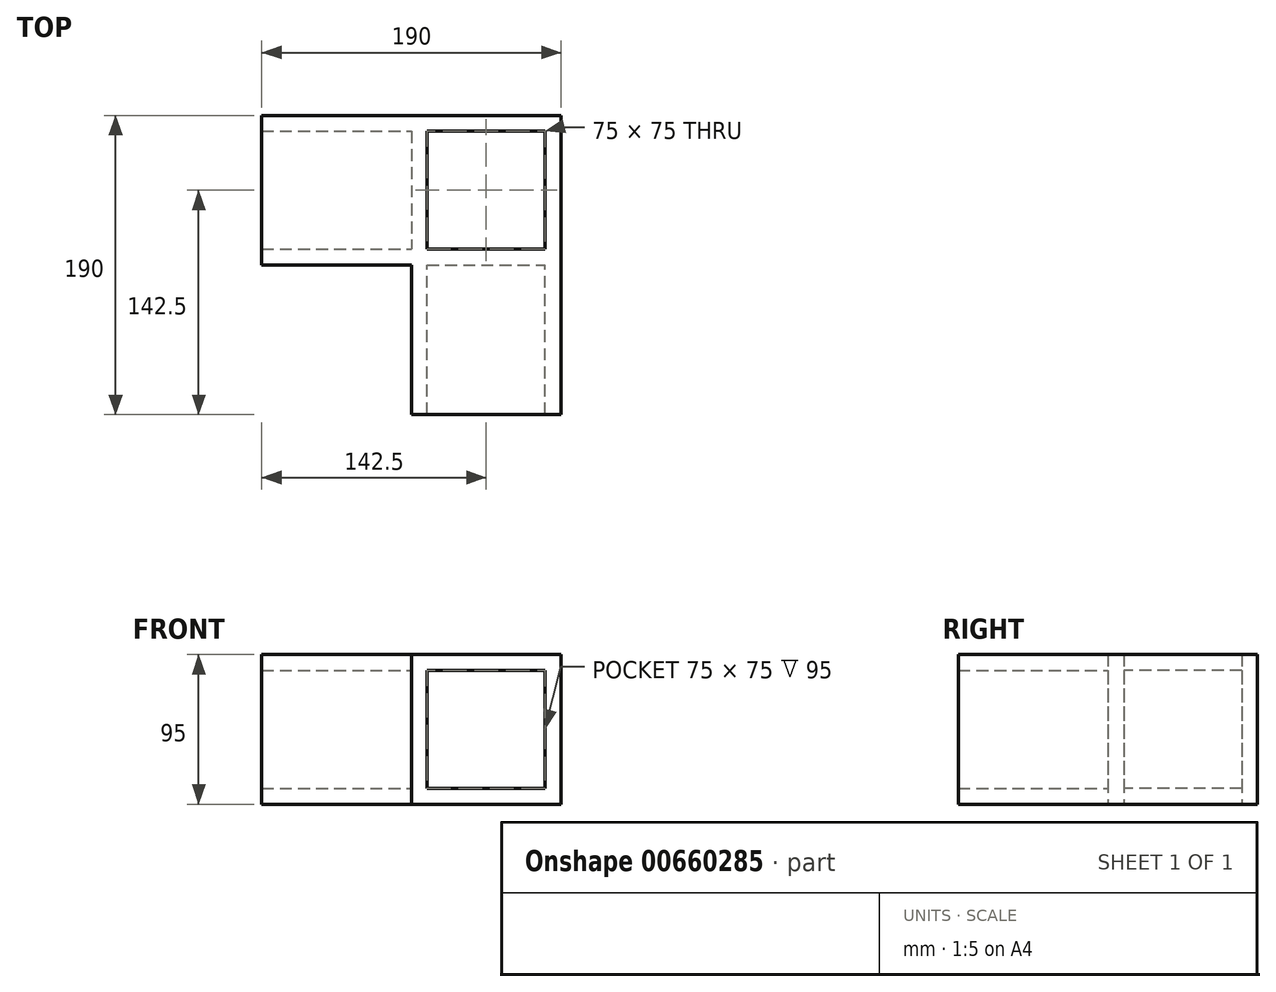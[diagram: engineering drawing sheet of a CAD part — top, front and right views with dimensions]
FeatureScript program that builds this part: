
annotation { "Feature Type Name" : "Feature", "Feature Type Description" : "" }
export const myFeature = defineFeature(function(context is Context, id is Id, definition is map)
    precondition{}
    {
        {
            var Q0;
            Q0=qCreatedBy(makeId("Top.planeOp"),FACE);
            var sketch = newSketch(context, id + "F0", { "sketchPlane" : qUnion([Q0])});
            skLineSegment(sketch, "E0.bottom", {"start": v(37.5, 37.5) * mm, "end": v(-37.5, 37.5) * mm});
            skLineSegment(sketch, "E0.top", {"start": v(37.5, -37.5) * mm, "end": v(-37.5, -37.5) * mm});
            skLineSegment(sketch, "E0.left", {"start": v(37.5, 37.5) * mm, "end": v(37.5, -37.5) * mm});
            skLineSegment(sketch, "E0.right", {"start": v(-37.5, 37.5) * mm, "end": v(-37.5, -37.5) * mm});
            skPoint(sketch, "E0.middle", {"position": v(0, 0) * mm});
            skLineSegment(sketch, "E1.bottom", {"start": v(47.5, 47.5) * mm, "end": v(-47.5, 47.5) * mm});
            skLineSegment(sketch, "E1.top", {"start": v(47.5, -47.5) * mm, "end": v(-47.5, -47.5) * mm});
            skLineSegment(sketch, "E1.left", {"start": v(47.5, 47.5) * mm, "end": v(47.5, -47.5) * mm});
            skLineSegment(sketch, "E1.right", {"start": v(-47.5, 47.5) * mm, "end": v(-47.5, -47.5) * mm});
            skSolve(sketch);
        }
        {
            var Q0;
            Q0 = qSketchRegion(id + "F0", true);
            extrude(context, id + "F1", {"entities" : qUnion([Q0]), "depth" : 95 * mm, "offsetDistance" : 25 * mm});
        }
        {
            var Q0;
            Q0=makeQuery(id+"F1.opExtrude","SWEPT_FACE",FACE,{"disambiguationData":[OSD([sQuery(id+"F0.wireOp",EDGE,"E1.top")])]});
            var sketch = newSketch(context, id + "F2", { "sketchPlane" : qUnion([Q0])});
            skLineSegment(sketch, "E2.bottom", {"start": v(-47.5, 95) * mm, "end": v(47.5, 95) * mm});
            skLineSegment(sketch, "E2.top", {"start": v(-47.5, 0) * mm, "end": v(47.5, 0) * mm});
            skLineSegment(sketch, "E2.left", {"start": v(-47.5, 95) * mm, "end": v(-47.5, 0) * mm});
            skLineSegment(sketch, "E2.right", {"start": v(47.5, 95) * mm, "end": v(47.5, 0) * mm});
            skLineSegment(sketch, "E3.0", {"start": v(-37.5, 85) * mm, "end": v(37.5, 85) * mm});
            skLineSegment(sketch, "E3.1", {"start": v(-37.5, 85) * mm, "end": v(-37.5, 10) * mm});
            skLineSegment(sketch, "E3.2", {"start": v(-37.5, 10) * mm, "end": v(37.5, 10) * mm});
            skLineSegment(sketch, "E3.3", {"start": v(37.5, 85) * mm, "end": v(37.5, 10) * mm});
            skSolve(sketch);
        }
        {
            var Q0;
            Q0 = qSketchRegion(id + "F2", true);
            extrude(context, id + "F3", {"entities" : qUnion([Q0]), "operationType" : NewBodyOperationType.ADD, "depth" : 95 * mm, "offsetDistance" : 25 * mm});
        }
        {
            var Q0;
            Q0=makeQuery(id+"F3.boolean.opBoolean","MERGE",FACE,{"derivedFrom":[makeQuery(id+"F1.opExtrude","SWEPT_FACE",FACE,{"disambiguationData":[OSD([sQuery(id+"F0.wireOp",EDGE,"E1.right")])]}),makeQuery(id+"F3.opExtrude","SWEPT_FACE",FACE,{"disambiguationData":[OSD([sQuery(id+"F2.wireOp",EDGE,"E2.left")])]})]});
            var sketch = newSketch(context, id + "F4", { "sketchPlane" : qUnion([Q0])});
            skLineSegment(sketch, "E4.bottom", {"start": v(-47.5, 95) * mm, "end": v(47.5, 95) * mm});
            skLineSegment(sketch, "E4.top", {"start": v(-47.5, 0) * mm, "end": v(47.5, 0) * mm});
            skLineSegment(sketch, "E4.left", {"start": v(-47.5, 95) * mm, "end": v(-47.5, 0) * mm});
            skLineSegment(sketch, "E4.right", {"start": v(47.5, 95) * mm, "end": v(47.5, 0) * mm});
            skLineSegment(sketch, "E5.0", {"start": v(-37.5, 85) * mm, "end": v(37.5, 85) * mm});
            skLineSegment(sketch, "E5.1", {"start": v(-37.5, 85) * mm, "end": v(-37.5, 10) * mm});
            skLineSegment(sketch, "E5.2", {"start": v(-37.5, 10) * mm, "end": v(37.5, 10) * mm});
            skLineSegment(sketch, "E5.3", {"start": v(37.5, 85) * mm, "end": v(37.5, 10) * mm});
            skSolve(sketch);
        }
        {
            var Q0;
            Q0 = qSketchRegion(id + "F4", true);
            extrude(context, id + "F5", {"entities" : qUnion([Q0]), "operationType" : NewBodyOperationType.ADD, "depth" : 95 * mm, "offsetDistance" : 25 * mm});
        }
    });
